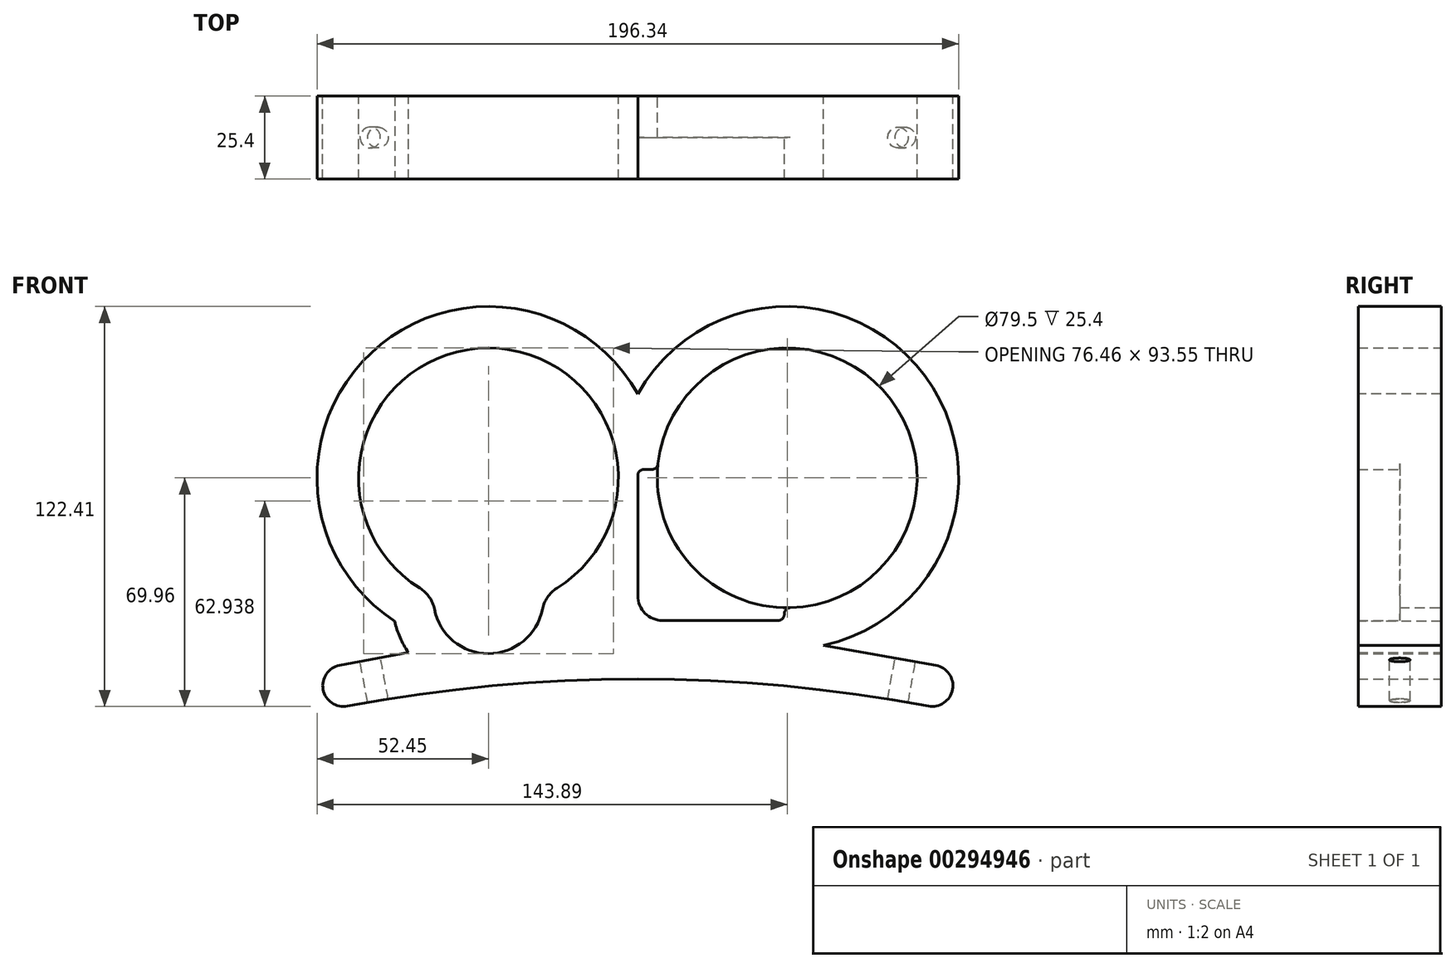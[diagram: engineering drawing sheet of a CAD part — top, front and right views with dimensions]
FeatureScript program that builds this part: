
annotation { "Feature Type Name" : "Feature", "Feature Type Description" : "" }
export const myFeature = defineFeature(function(context is Context, id is Id, definition is map)
    precondition{}
    {
        {
            var Q0;
            Q0=qCreatedBy(makeId("Front.planeOp"),FACE);
            var sketch = newSketch(context, id + "F0", { "sketchPlane" : qUnion([Q0])});
            skArc(sketch, "E0", {"start": v(88.9, 0) * mm, "mid": v(0, 8.26) * mm, "end": v(-88.9, 0) * mm});
            skCircle(sketch, "E1", {"center": v(45.72, 69.85) * mm, "radius": 39.75 * mm});
            skCircle(sketch, "E2.0", {"center": v(45.72, 69.85) * mm, "radius": 52.45 * mm});
            skPoint(sketch, "E3.MirrorCS.start.orphan", {"position": v(54.2, 6.84) * mm});
            skPoint(sketch, "E4.start.orphan", {"position": v(-101.42, -8.26) * mm});
            skPoint(sketch, "E5.start.orphan", {"position": v(-98.5, -17.4) * mm});
            skPoint(sketch, "E6.start.orphan", {"position": v(-50.51, -2.07) * mm});
            skPoint(sketch, "E7.start.orphan", {"position": v(-54.2, 6.84) * mm});
            skPoint(sketch, "E8.MirrorCS.start.orphan", {"position": v(50.51, -2.07) * mm});
            skPoint(sketch, "E9.MirrorCS.start.orphan", {"position": v(98.5, -17.4) * mm});
            skPoint(sketch, "E10.start.orphan", {"position": v(101.42, -8.26) * mm});
            skPoint(sketch, "E11.middle", {"position": v(-45.72, 69.85) * mm});
            skPoint(sketch, "E11.right.start.orphan", {"position": v(-83.82, 31.75) * mm});
            skArc(sketch, "E12", {"start": v(-28.92, 33.82) * mm, "mid": v(-45.72, 109.6) * mm, "end": v(-62.52, 33.82) * mm});
            skArc(sketch, "E13", {"start": v(-62.52, 33.82) * mm, "mid": v(-45.72, 16.05) * mm, "end": v(-28.92, 33.82) * mm});
            skArc(sketch, "E14.0", {"start": v(-29.1, 20.1) * mm, "mid": v(-39.01, 121.87) * mm, "end": v(-74.42, 25.95) * mm});
            skArc(sketch, "E14.1", {"start": v(-74.42, 25.95) * mm, "mid": v(-72.65, 20.76) * mm, "end": v(-69.94, 16) * mm});
            skPoint(sketch, "E15.trimOffspring.end.orphan", {"position": v(-83.82, 107.95) * mm});
            skPoint(sketch, "E16.orphan", {"position": v(-7.62, 107.95) * mm});
            skPoint(sketch, "E17.orphan", {"position": v(-7.62, 31.75) * mm});
            skPoint(sketch, "E18.left.start.orphan", {"position": v(168.3, 9.64) * mm});
            skPoint(sketch, "E19.trimOffspring.end.orphan", {"position": v(88.9, 113.03) * mm});
            skPoint(sketch, "E20.orphan", {"position": v(-76.86, 130.06) * mm});
            skPoint(sketch, "E18.right.start.orphan", {"position": v(2.54, 26.67) * mm});
            skPoint(sketch, "E21.end.orphan", {"position": v(168.3, -1295.47) * mm});
            skArc(sketch, "E22.0", {"start": v(91.24, 12.48) * mm, "mid": v(0, 20.96) * mm, "end": v(-91.24, 12.48) * mm});
            skArc(sketch, "E23", {"start": v(-88.9, 0) * mm, "mid": v(-96.31, 5.07) * mm, "end": v(-91.24, 12.48) * mm});
            skArc(sketch, "E24", {"start": v(88.9, 0) * mm, "mid": v(96.31, 5.07) * mm, "end": v(91.24, 12.48) * mm});
            skCircle(sketch, "E25", {"center": v(7.62, 33.8) * mm, "radius": 7.62 * mm});
            skLineSegment(sketch, "E26", {"start": v(0, 33.8) * mm, "end": v(0, 72.45) * mm});
            skLineSegment(sketch, "E27", {"start": v(44.83, 26.18) * mm, "end": v(7.62, 26.18) * mm});
            skLineSegment(sketch, "E28", {"start": v(-91.24, 12.48) * mm, "end": v(-70.23, 16.42) * mm});
            skLineSegment(sketch, "E29", {"start": v(91.24, 12.48) * mm, "end": v(56.87, 18.6) * mm});
            skLineSegment(sketch, "E30", {"start": v(0, 72.45) * mm, "end": v(6.05, 72.45) * mm});
            skLineSegment(sketch, "E31", {"start": v(44.83, 26.18) * mm, "end": v(44.83, 30.1) * mm});
            skLineSegment(sketch, "E32", {"start": v(-45.72, 69.85) * mm, "end": v(-45.72, -4.09) * mm, "construction": true});
            skSolve(sketch);
        }
        {
            var Q0;
            {var subQ0=sQuery(id+"F0.wireOp",EDGE,"E22.0");var subQ1=sQuery(id+"F0.wireOp",EDGE,"E2.0");var subQ2=makeQuery(id+"F0.imprint","INTERSECT",VERTEX,{"disambiguationData":[OD(0.0)],"derivedFrom":[subQ1,subQ0]});Q0=makeQuery(id+"F0.imprint","IMPRINT",FACE,{"disambiguationData":[TD([[makeQuery(id+"F0.imprint","IMPRINT",EDGE,{"disambiguationData":[TD([[subQ2,1.0]])],"derivedFrom":subQ1}),1.0]])]});}
            var Q1;
            {var subQ0=sQuery(id+"F0.wireOp",EDGE,"E22.0");var subQ1=sQuery(id+"F0.wireOp",EDGE,"E14.1");var subQ2=makeQuery(id+"F0.imprint","INTERSECT",VERTEX,{"disambiguationData":[OD(0.0)],"derivedFrom":[subQ1,subQ0]});Q1=makeQuery(id+"F0.imprint","IMPRINT",FACE,{"disambiguationData":[TD([[makeQuery(id+"F0.imprint","IMPRINT",EDGE,{"disambiguationData":[TD([[subQ2,-1.0]])],"derivedFrom":subQ1}),1.0]])]});}
            var Q2;
            Q2=makeQuery(id+"F0.imprint","IMPRINT",FACE,{"disambiguationData":[TD([[makeQuery(id+"F0.imprint","IMPRINT",EDGE,{"derivedFrom":sQuery(id+"F0.wireOp",EDGE,"E0")}),-1.0]])]});
            var Q3;
            Q3=makeQuery(id+"F0.imprint","IMPRINT",FACE,{"disambiguationData":[TD([[makeQuery(id+"F0.imprint","IMPRINT",EDGE,{"derivedFrom":sQuery(id+"F0.wireOp",EDGE,"E12")}),-1.0]])]});
            var Q4;
            {var subQ10=sQuery(id+"F0.wireOp",EDGE,"E26");Q4=makeQuery(id+"F0.imprint","IMPRINT",FACE,{"disambiguationData":[TD([[makeQuery(id+"F0.imprint","IMPRINT",EDGE,{"derivedFrom":subQ10}),1.0]])]});}
            var Q5;
            {var subQ0=sQuery(id+"F0.wireOp",EDGE,"E14.0");var subQ1=sQuery(id+"F0.wireOp",EDGE,"E2.0");var subQ2=makeQuery(id+"F0.imprint","INTERSECT",VERTEX,{"disambiguationData":[OD(0.0)],"derivedFrom":[subQ1,subQ0]});Q5=makeQuery(id+"F0.imprint","IMPRINT",FACE,{"disambiguationData":[TD([[makeQuery(id+"F0.imprint","IMPRINT",EDGE,{"disambiguationData":[TD([[subQ2,-1.0]])],"derivedFrom":subQ1}),1.0]])]});}
            var Q6;
            {var subQ0=sQuery(id+"F0.wireOp",EDGE,"E14.1");var subQ1=sQuery(id+"F0.wireOp",EDGE,"E14.0");var subQ2=makeQuery(id+"F0.imprint","INTERSECT",VERTEX,{"disambiguationData":[OD(0.0)],"derivedFrom":[subQ1,subQ0]});Q6=makeQuery(id+"F0.imprint","IMPRINT",FACE,{"disambiguationData":[TD([[makeQuery(id+"F0.imprint","IMPRINT",EDGE,{"disambiguationData":[TD([[subQ2,-1.0]])],"derivedFrom":subQ1}),-1.0]])]});}
            var Q7;
            {var subQ0=sQuery(id+"F0.wireOp",EDGE,"E22.0");var subQ1=sQuery(id+"F0.wireOp",EDGE,"E14.0");var subQ2=makeQuery(id+"F0.imprint","INTERSECT",VERTEX,{"disambiguationData":[OD(0.0)],"derivedFrom":[subQ1,subQ0]});Q7=makeQuery(id+"F0.imprint","IMPRINT",FACE,{"disambiguationData":[TD([[makeQuery(id+"F0.imprint","IMPRINT",EDGE,{"disambiguationData":[TD([[subQ2,-1.0]])],"derivedFrom":subQ1}),1.0]])]});}
            var Q8;
            {var subQ0=sQuery(id+"F0.wireOp",EDGE,"b9e1950e-4711-4437-b9bd-60db70ccd0c8.0");Q8=makeQuery(id+"F0.imprint","IMPRINT",FACE,{"disambiguationData":[TD([[makeQuery(id+"F0.imprint","IMPRINT",EDGE,{"derivedFrom":subQ0}),-1.0]])]});}
            var Q9;
            {var subQ0=sQuery(id+"F0.wireOp",EDGE,"E28");Q9=makeQuery(id+"F0.imprint","IMPRINT",FACE,{"disambiguationData":[TD([[makeQuery(id+"F0.imprint","IMPRINT",EDGE,{"derivedFrom":subQ0}),-1.0]])]});}
            var Q10;
            {var subQ0=sQuery(id+"F0.wireOp",EDGE,"E22.0");var subQ1=sQuery(id+"F0.wireOp",EDGE,"E2.0");var subQ2=makeQuery(id+"F0.imprint","INTERSECT",VERTEX,{"disambiguationData":[OD(0.0)],"derivedFrom":[subQ1,subQ0]});Q10=makeQuery(id+"F0.imprint","IMPRINT",FACE,{"disambiguationData":[TD([[makeQuery(id+"F0.imprint","IMPRINT",EDGE,{"disambiguationData":[TD([[subQ2,-1.0]])],"derivedFrom":subQ1}),1.0]])]});}
            var Q11;
            {var subQ0=sQuery(id+"F0.wireOp",EDGE,"E29");var subQ1=sQuery(id+"F0.wireOp",EDGE,"E2.0");var subQ2=makeQuery(id+"F0.imprint","INTERSECT",VERTEX,{"derivedFrom":[subQ1,subQ0]});Q11=makeQuery(id+"F0.imprint","IMPRINT",FACE,{"disambiguationData":[TD([[makeQuery(id+"F0.imprint","IMPRINT",EDGE,{"disambiguationData":[TD([[subQ2,1.0]])],"derivedFrom":subQ1}),-1.0]])]});}
            extrude(context, id + "F1", {"entities" : qUnion([Q0, Q1, Q2, Q3, Q4, Q5, Q6, Q7, Q8, Q9, Q10, Q11]), "endBound" : BoundingType.SYMMETRIC, "depth" : 25.4 * mm});
        }
        {
            var Q0;
            {var subQ0=sQuery(id+"F0.wireOp",EDGE,"E26");Q0=makeQuery(id+"F0.imprint","IMPRINT",FACE,{"disambiguationData":[TD([[makeQuery(id+"F0.imprint","IMPRINT",EDGE,{"derivedFrom":subQ0}),-1.0]])]});}
            var Q1;
            {var subQ0=sQuery(id+"F0.wireOp",EDGE,"E25");var subQ4=sQuery(id+"F0.wireOp",EDGE,"E1");var subQ5=makeQuery(id+"F0.imprint","INTERSECT",VERTEX,{"disambiguationData":[OD(0.0)],"derivedFrom":[subQ4,subQ0]});Q1=makeQuery(id+"F0.imprint","IMPRINT",FACE,{"disambiguationData":[TD([[makeQuery(id+"F0.imprint","IMPRINT",EDGE,{"disambiguationData":[TD([[subQ5,-1.0]])],"derivedFrom":subQ4}),-1.0]])]});}
            var Q2;
            {var subQ0=sQuery(id+"F0.wireOp",EDGE,"E27");Q2=makeQuery(id+"F0.imprint","IMPRINT",FACE,{"disambiguationData":[TD([[makeQuery(id+"F0.imprint","IMPRINT",EDGE,{"derivedFrom":subQ0}),-1.0]])]});}
            var Q3;
            {var subQ0=sQuery(id+"F0.wireOp",EDGE,"E25");var subQ1=sQuery(id+"F0.wireOp",EDGE,"E2.0");var subQ2=makeQuery(id+"F0.imprint","INTERSECT",VERTEX,{"disambiguationData":[OD(0.0)],"derivedFrom":[subQ1,subQ0]});Q3=makeQuery(id+"F0.imprint","IMPRINT",FACE,{"disambiguationData":[TD([[makeQuery(id+"F0.imprint","IMPRINT",EDGE,{"disambiguationData":[TD([[subQ2,-1.0]])],"derivedFrom":subQ1}),-1.0]])]});}
            var Q4;
            {var subQ10=sQuery(id+"F0.wireOp",EDGE,"E31");Q4=makeQuery(id+"F0.imprint","IMPRINT",FACE,{"disambiguationData":[TD([[makeQuery(id+"F0.imprint","IMPRINT",EDGE,{"derivedFrom":subQ10}),1.0]])]});}
            var Q5;
            {var subQ0=sQuery(id+"F0.wireOp",EDGE,"E25");var subQ1=sQuery(id+"F0.wireOp",EDGE,"E2.0");var subQ2=makeQuery(id+"F0.imprint","INTERSECT",VERTEX,{"disambiguationData":[OD(0.0)],"derivedFrom":[subQ1,subQ0]});Q5=makeQuery(id+"F0.imprint","IMPRINT",FACE,{"disambiguationData":[TD([[makeQuery(id+"F0.imprint","IMPRINT",EDGE,{"disambiguationData":[TD([[subQ2,-1.0]])],"derivedFrom":subQ1}),1.0]])]});}
            var Q6;
            {var subQ0=sQuery(id+"F0.wireOp",EDGE,"E30");Q6=makeQuery(id+"F0.imprint","IMPRINT",FACE,{"disambiguationData":[TD([[makeQuery(id+"F0.imprint","IMPRINT",EDGE,{"derivedFrom":subQ0}),-1.0]])]});}
            var Q7;
            {var subQ0=sQuery(id+"F0.wireOp",EDGE,"E14.0");var subQ1=sQuery(id+"F0.wireOp",EDGE,"E2.0");var subQ2=makeQuery(id+"F0.imprint","INTERSECT",VERTEX,{"disambiguationData":[OD(1.0)],"derivedFrom":[subQ1,subQ0]});Q7=makeQuery(id+"F0.imprint","IMPRINT",FACE,{"disambiguationData":[TD([[makeQuery(id+"F0.imprint","IMPRINT",EDGE,{"disambiguationData":[TD([[subQ2,-1.0]])],"derivedFrom":subQ1}),-1.0]])]});}
            extrude(context, id + "F2", {"entities" : qUnion([Q0, Q1, Q2, Q3, Q4, Q5, Q6, Q7]), "operationType" : NewBodyOperationType.ADD, "oppositeDirection" : true, "depth" : 12.7 * mm});
        }
        {
            var Q0;
            Q0=makeQuery(id+"F1.opExtrude","SWEPT_FACE",FACE,{"disambiguationData":[OSD([sQuery(id+"F0.wireOp",EDGE,"E29")])]});
            var sketch = newSketch(context, id + "F3", { "sketchPlane" : qUnion([Q0])});
            skCircle(sketch, "E33", {"center": v(78.12, 0) * mm, "radius": 3.17 * mm});
            skSolve(sketch);
        }
        {
            var Q0;
            Q0=qSketchRegion(id+"F3",true);
            extrude(context, id + "F4", {"entities" : qUnion([Q0]), "operationType" : NewBodyOperationType.REMOVE, "endBound" : BoundingType.SYMMETRIC, "oppositeDirection" : true, "depth" : 30.48 * mm});
        }
        {
            var Q0;
            Q0=makeQuery(id+"F1.opExtrude","SWEPT_FACE",FACE,{"disambiguationData":[OSD([sQuery(id+"F0.wireOp",EDGE,"E28")])]});
            var sketch = newSketch(context, id + "F5", { "sketchPlane" : qUnion([Q0])});
            skCircle(sketch, "E34", {"center": v(-77.85, 0) * mm, "radius": 3.18 * mm});
            skSolve(sketch);
        }
        {
            var Q0;
            Q0=qSketchRegion(id+"F5",true);
            extrude(context, id + "F6", {"entities" : qUnion([Q0]), "operationType" : NewBodyOperationType.REMOVE, "endBound" : BoundingType.SYMMETRIC, "oppositeDirection" : true, "depth" : 36.58 * mm});
        }
        {
            var Q0;
            {var subQ0=sQuery(id+"F0.wireOp",EDGE,"E14.0");var subQ2=sQuery(id+"F0.wireOp",EDGE,"E2.0");var subQ3=makeQuery(id+"F0.imprint","INTERSECT",VERTEX,{"disambiguationData":[OD(0.0)],"derivedFrom":[subQ2,subQ0]});Q0=makeQuery(id+"F0.imprint","IMPRINT",FACE,{"disambiguationData":[TD([[makeQuery(id+"F0.imprint","IMPRINT",EDGE,{"disambiguationData":[TD([[subQ3,-1.0]])],"derivedFrom":subQ2}),-1.0]])]});}
            extrude(context, id + "F7", {"entities" : qUnion([Q0]), "operationType" : NewBodyOperationType.ADD, "endBound" : BoundingType.SYMMETRIC, "depth" : 25.4 * mm});
        }
        {
            var Q0;
            Q0=makeQuery(id+"F1.opExtrude","SWEPT_EDGE",EDGE,{"disambiguationData":[OSD([sQuery(id+"F0.wireOp",EDGE,"E1"),sQuery(id+"F0.wireOp",EDGE,"E30")])]});
            var Q1;
            Q1=makeQuery(id+"F1.opExtrude","SWEPT_EDGE",EDGE,{"disambiguationData":[OSD([sQuery(id+"F0.wireOp",EDGE,"E26"),sQuery(id+"F0.wireOp",EDGE,"E30")])]});
            var Q2;
            Q2=makeQuery(id+"F1.opExtrude","SWEPT_EDGE",EDGE,{"disambiguationData":[OSD([sQuery(id+"F0.wireOp",EDGE,"E1"),sQuery(id+"F0.wireOp",EDGE,"E31")])]});
            var Q3;
            Q3=makeQuery(id+"F1.opExtrude","SWEPT_EDGE",EDGE,{"disambiguationData":[OSD([sQuery(id+"F0.wireOp",EDGE,"E27"),sQuery(id+"F0.wireOp",EDGE,"E31")])]});
            fillet(context, id + "F8", {"entities" : qUnion([Q0, Q1, Q2, Q3]), "radius" : 1.9 * mm, "tangentPropagation" : true, "allowEdgeOverflow" : false});
        }
        {
            var Q0;
            {var subQ0=sQuery(id+"F0.wireOp",EDGE,"E13");var subQ1=sQuery(id+"F0.wireOp",EDGE,"E12");Q0=makeQuery(id+"F7.boolean.opBoolean","MERGE",EDGE,{"derivedFrom":[makeQuery(id+"F2.opExtrude","SWEPT_EDGE",EDGE,{"disambiguationData":[OSD([subQ1,subQ0])]}),makeQuery(id+"F7.opExtrude","SWEPT_EDGE",EDGE,{"disambiguationData":[OSD([subQ1,subQ0])]})]});}
            var Q1;
            Q1=makeQuery(id+"F1.opExtrude","SWEPT_EDGE",EDGE,{"disambiguationData":[OSD([sQuery(id+"F0.wireOp",EDGE,"E12"),sQuery(id+"F0.wireOp",EDGE,"E13")])]});
            fillet(context, id + "F9", {"entities" : qUnion([Q0, Q1]), "radius" : 9.78 * mm, "tangentPropagation" : true, "allowEdgeOverflow" : false});
        }
    });
